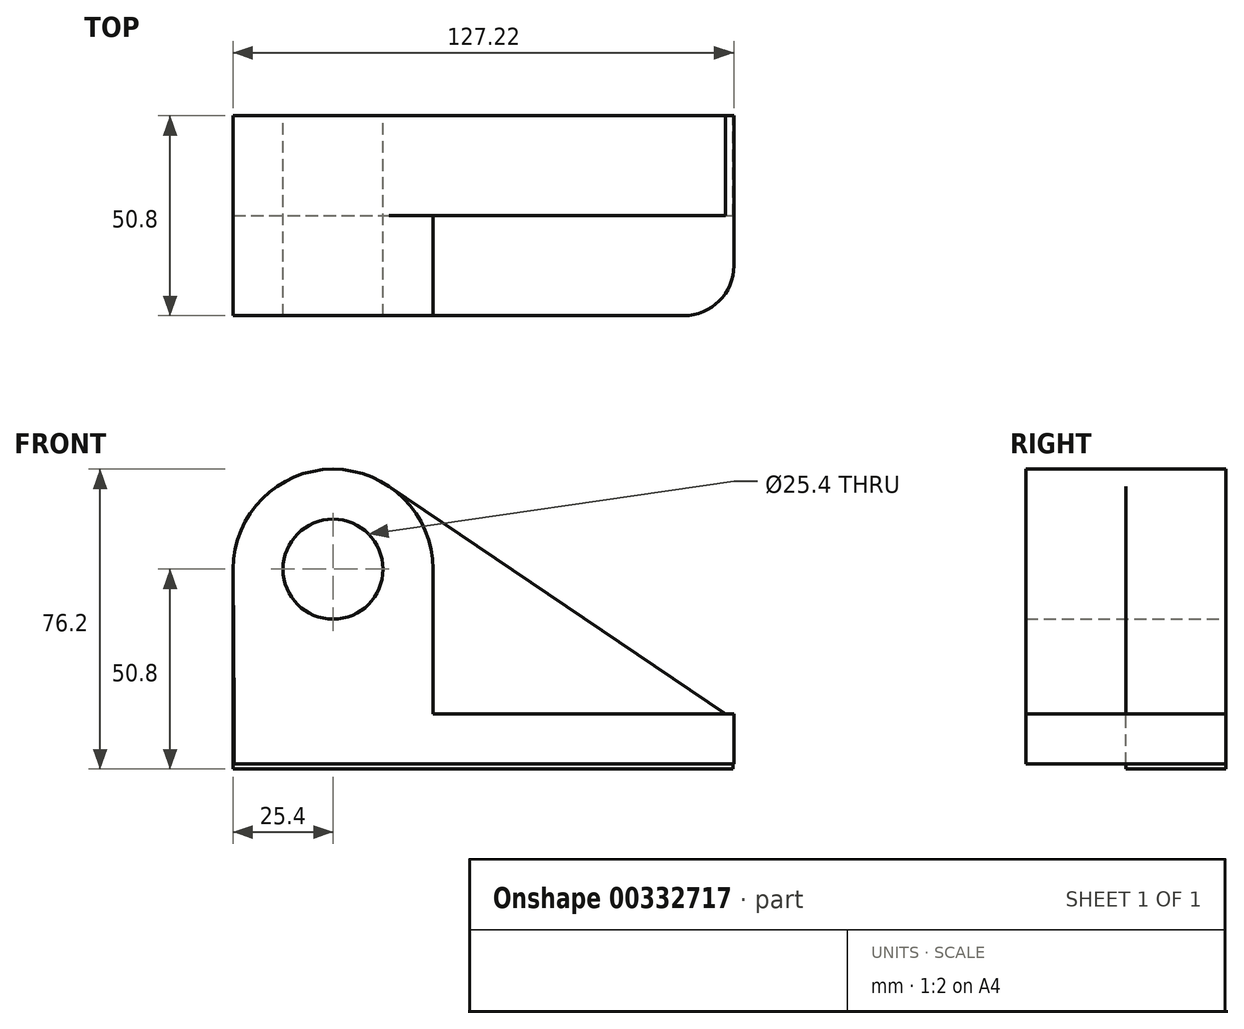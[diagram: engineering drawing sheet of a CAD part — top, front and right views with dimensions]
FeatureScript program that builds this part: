
annotation { "Feature Type Name" : "Feature", "Feature Type Description" : "" }
export const myFeature = defineFeature(function(context is Context, id is Id, definition is map)
    precondition{}
    {
        {
            var Q0;
            Q0=qCreatedBy(makeId("Front.planeOp"),FACE);
            var sketch = newSketch(context, id + "F0", { "sketchPlane" : qUnion([Q0])});
            skCircle(sketch, "E0", {"center": v(0, 0) * mm, "radius": 12.7 * mm});
            skArc(sketch, "E1", {"start": v(14.24, 21.03) * mm, "mid": v(-11.9, 22.44) * mm, "end": v(-25.4, 0) * mm});
            skLineSegment(sketch, "E2", {"start": v(-25.4, 0) * mm, "end": v(-25.4, -50.8) * mm});
            skLineSegment(sketch, "E3", {"start": v(-25.4, -50.8) * mm, "end": v(101.6, -50.8) * mm});
            skLineSegment(sketch, "E4", {"start": v(101.6, -50.8) * mm, "end": v(101.6, -38.1) * mm});
            skLineSegment(sketch, "E5", {"start": v(101.6, -38.1) * mm, "end": v(14.24, 21.03) * mm});
            skSolve(sketch);
        }
        {
            var Q0;
            Q0 = qSketchRegion(id + "F0", true);
            extrude(context, id + "F1", {"entities" : qUnion([Q0]), "depth" : 25.4 * mm});
        }
        {
            var Q0;
            Q0=qCreatedBy(makeId("Front.planeOp"),FACE);
            var sketch = newSketch(context, id + "F2", { "sketchPlane" : qUnion([Q0])});
            skCircle(sketch, "E6", {"center": v(0, 0) * mm, "radius": 12.7 * mm});
            skArc(sketch, "E7", {"start": v(25.4, 0) * mm, "mid": v(0, 25.4) * mm, "end": v(-25.4, 0) * mm});
            skLineSegment(sketch, "E8.bottom", {"start": v(101.82, -36.83) * mm, "end": v(25.4, -36.83) * mm});
            skLineSegment(sketch, "E8.top", {"start": v(101.82, -49.53) * mm, "end": v(-25.18, -49.53) * mm});
            skLineSegment(sketch, "E8.left", {"start": v(101.82, -36.83) * mm, "end": v(101.82, -49.53) * mm});
            skLineSegment(sketch, "E9", {"start": v(25.4, 0) * mm, "end": v(25.4, -36.83) * mm});
            skPoint(sketch, "E10.start.orphan", {"position": v(-25.4, 0) * mm});
            skLineSegment(sketch, "E11", {"start": v(-25.18, -36.83) * mm, "end": v(-25.18, -49.53) * mm});
            skLineSegment(sketch, "E12", {"start": v(-25.4, 0) * mm, "end": v(-25.18, -36.83) * mm});
            skSolve(sketch);
        }
        {
            var Q0;
            Q0=makeQuery(id+"F2.imprint","IMPRINT",FACE,{"disambiguationData":[TD([[makeQuery(id+"F2.imprint","IMPRINT",EDGE,{"derivedFrom":sQuery(id+"F2.wireOp",EDGE,"E6")}),-1.0]])]});
            extrude(context, id + "F3", {"entities" : qUnion([Q0]), "operationType" : NewBodyOperationType.ADD, "depth" : 50.8 * mm});
        }
        {
            var Q0;
            Q0=makeQuery(id+"F3.opExtrude","CAP_EDGE",EDGE,{"disambiguationData":[OSD([sQuery(id+"F2.wireOp",EDGE,"E8.left")])],"isStart":false});
            fillet(context, id + "F4", {"entities" : qUnion([Q0]), "radius" : 12.7 * mm, "tangentPropagation" : true, "allowEdgeOverflow" : false});
        }
    });
